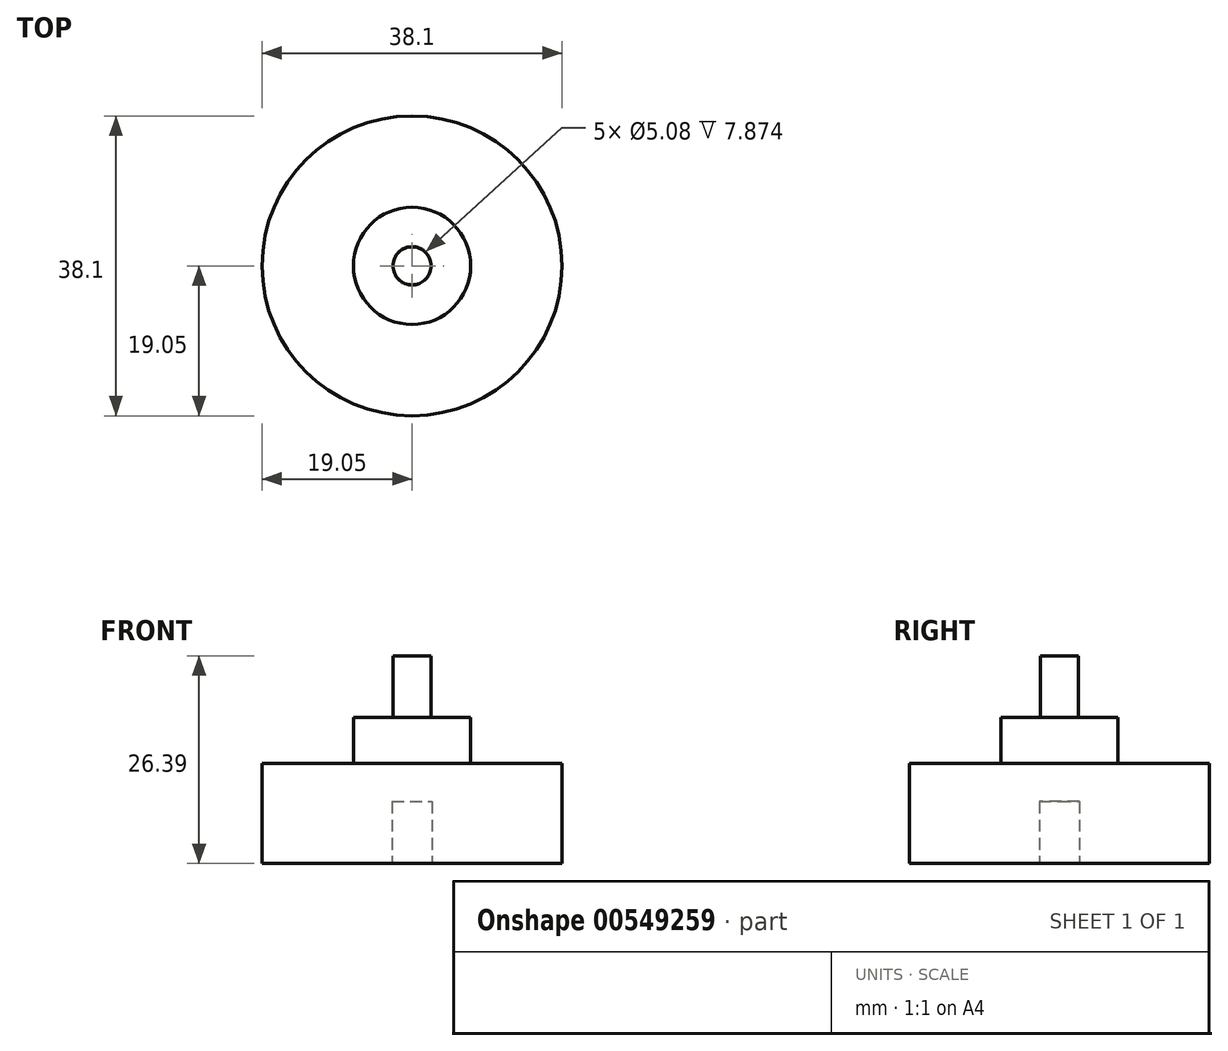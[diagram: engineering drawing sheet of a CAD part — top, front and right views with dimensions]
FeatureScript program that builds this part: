
annotation { "Feature Type Name" : "Feature", "Feature Type Description" : "" }
export const myFeature = defineFeature(function(context is Context, id is Id, definition is map)
    precondition{}
    {
        {
            var Q0;
            Q0=qCreatedBy(makeId("Front.planeOp"),FACE);
            var sketch = newSketch(context, id + "F0", { "sketchPlane" : qUnion([Q0])});
            skLineSegment(sketch, "E0", {"start": v(0, 0) * mm, "end": v(19.05, 0) * mm});
            skLineSegment(sketch, "E1", {"start": v(19.05, 0) * mm, "end": v(19.05, 12.7) * mm});
            skLineSegment(sketch, "E2", {"start": v(19.05, 12.7) * mm, "end": v(7.44, 12.7) * mm});
            skLineSegment(sketch, "E3", {"start": v(2.41, 18.54) * mm, "end": v(7.44, 18.54) * mm});
            skLineSegment(sketch, "E4", {"start": v(7.44, 18.54) * mm, "end": v(7.44, 12.7) * mm});
            skLineSegment(sketch, "E5", {"start": v(0, 0) * mm, "end": v(2.54, 0) * mm});
            skLineSegment(sketch, "E6", {"start": v(2.54, 0) * mm, "end": v(2.54, 7.87) * mm});
            skLineSegment(sketch, "E7", {"start": v(2.54, 7.87) * mm, "end": v(0, 7.87) * mm});
            skLineSegment(sketch, "E8", {"start": v(0, 26.4) * mm, "end": v(2.41, 26.4) * mm});
            skLineSegment(sketch, "E9", {"start": v(2.41, 26.4) * mm, "end": v(2.41, 18.54) * mm});
            skLineSegment(sketch, "E10", {"start": v(0, 7.87) * mm, "end": v(0, 26.4) * mm});
            skSolve(sketch);
        }
        {
            var Q0;
            Q0 = qSketchRegion(id + "F0", true);
            var Q1;
            Q1=sQuery(id+"F0.wireOp",EDGE,"E10");
            revolve(context, id + "F1", {"entities" : qUnion([Q0]), "axis" : qUnion([Q1]), "revolveType" : RevolveType.FULL});
        }
    });
